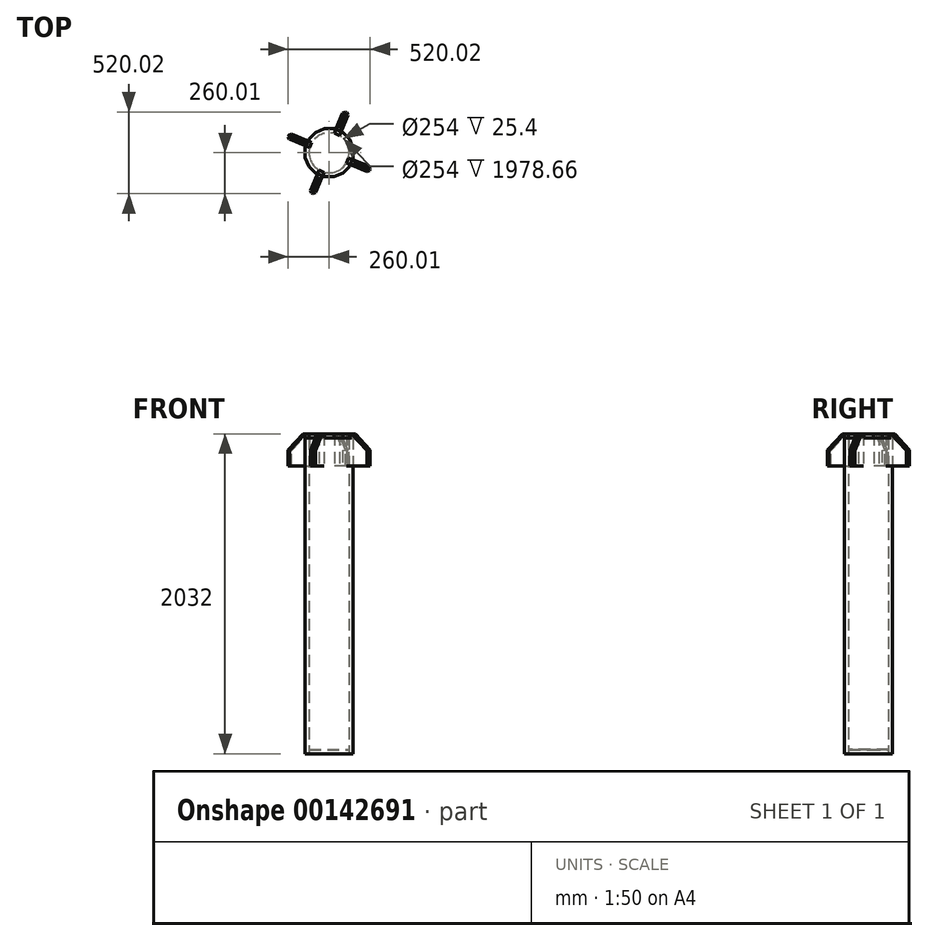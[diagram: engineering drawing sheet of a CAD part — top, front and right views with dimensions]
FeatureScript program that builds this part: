
annotation { "Feature Type Name" : "Feature", "Feature Type Description" : "" }
export const myFeature = defineFeature(function(context is Context, id is Id, definition is map)
    precondition{}
    {
        {
            var Q0;
            Q0=qCreatedBy(makeId("Top.planeOp"),FACE);
            var sketch = newSketch(context, id + "F0", { "sketchPlane" : qUnion([Q0])});
            skCircle(sketch, "E0", {"center": v(0, 0) * mm, "radius": 152.4 * mm});
            skCircle(sketch, "E1", {"center": v(0, 0) * mm, "radius": 151.13 * mm});
            skSolve(sketch);
        }
        {
            var Q0;
            Q0 = qSketchRegion(id + "F0", true);
            var Q1;
            Q1=makeQuery(id+"F0.imprint","IMPRINT",FACE,{"disambiguationData":[TD([[makeQuery(id+"F0.imprint","IMPRINT",EDGE,{"derivedFrom":sQuery(id+"F0.wireOp",EDGE,"E1")}),1.0]])]});
            extrude(context, id + "F1", {"entities" : qUnion([Q0, Q1]), "depth" : 2032 * mm});
        }
        {
            var Q0;
            Q0=makeQuery(id+"F1.opExtrude","CAP_FACE",FACE,{"disambiguationData":[OSD([sQuery(id+"F0.wireOp",EDGE,"E0")])],"isStart":true});
            shell(context, id + "F2", {"entities" : qUnion([Q0]), "thickness" : 25.4 * mm});
        }
        {
            var Q0;
            Q0=makeQuery(id+"F1.opExtrude","CAP_FACE",FACE,{"disambiguationData":[OSD([sQuery(id+"F0.wireOp",EDGE,"E0")])],"isStart":true});
            cPlane(context, id + "F3", {"entities" : qUnion([Q0]), "cplaneType" : CPlaneType.OFFSET, "offset" : 25.4 * mm, "oppositeDirection" : true, "width" : 152.4 * mm, "height" : 152.4 * mm});
        }
        {
            var Q0;
            Q0=qCreatedBy(id+"F3.planeOp",FACE);
            var sketch = newSketch(context, id + "F4", { "sketchPlane" : qUnion([Q0])});
            skCircle(sketch, "E2", {"center": v(0, 0) * mm, "radius": 152.4 * mm});
            skSolve(sketch);
        }
        {
            var Q0;
            Q0 = qSketchRegion(id + "F4", true);
            extrude(context, id + "F5", {"entities" : qUnion([Q0]), "operationType" : NewBodyOperationType.ADD, "oppositeDirection" : true, "depth" : 2.54 * mm});
        }
        {
            var Q0;
            Q0=makeQuery(id+"F1.opExtrude","CAP_FACE",FACE,{"disambiguationData":[OSD([sQuery(id+"F0.wireOp",EDGE,"E0")])],"isStart":false});
            var sketch = newSketch(context, id + "F6", { "sketchPlane" : qUnion([Q0])});
            skCircle(sketch, "E3.cCircle", {"center": v(0, 0) * mm, "radius": 152.4 * mm, "construction": true});
            skLineSegment(sketch, "E3.0", {"start": v(-152.4, -30.31) * mm, "end": v(-152.4, 30.31) * mm});
            skLineSegment(sketch, "E3.1", {"start": v(-152.4, 30.31) * mm, "end": v(-129.2, 86.33) * mm});
            skLineSegment(sketch, "E3.2", {"start": v(-129.2, 86.33) * mm, "end": v(-86.33, 129.2) * mm});
            skLineSegment(sketch, "E3.3", {"start": v(-86.33, 129.2) * mm, "end": v(-30.31, 152.4) * mm});
            skLineSegment(sketch, "E3.4", {"start": v(-30.31, 152.4) * mm, "end": v(30.31, 152.4) * mm});
            skLineSegment(sketch, "E3.5", {"start": v(30.31, 152.4) * mm, "end": v(86.33, 129.2) * mm});
            skLineSegment(sketch, "E3.6", {"start": v(86.33, 129.2) * mm, "end": v(129.2, 86.33) * mm});
            skLineSegment(sketch, "E3.7", {"start": v(129.2, 86.33) * mm, "end": v(152.4, 30.31) * mm});
            skLineSegment(sketch, "E3.8", {"start": v(152.4, 30.31) * mm, "end": v(152.4, -30.31) * mm});
            skLineSegment(sketch, "E3.9", {"start": v(152.4, -30.31) * mm, "end": v(129.2, -86.33) * mm});
            skLineSegment(sketch, "E3.10", {"start": v(129.2, -86.33) * mm, "end": v(86.33, -129.2) * mm});
            skLineSegment(sketch, "E3.11", {"start": v(86.33, -129.2) * mm, "end": v(30.31, -152.4) * mm});
            skLineSegment(sketch, "E3.12", {"start": v(30.31, -152.4) * mm, "end": v(-30.31, -152.4) * mm});
            skLineSegment(sketch, "E3.13", {"start": v(-30.31, -152.4) * mm, "end": v(-86.33, -129.2) * mm});
            skLineSegment(sketch, "E3.14", {"start": v(-86.33, -129.2) * mm, "end": v(-129.2, -86.33) * mm});
            skLineSegment(sketch, "E3.15", {"start": v(-129.2, -86.33) * mm, "end": v(-152.4, -30.31) * mm});
            skPoint(sketch, "E3.0.midPoint", {"position": v(-152.4, 0) * mm});
            skSolve(sketch);
        }
        {
            var Q0;
            Q0 = qSketchRegion(id + "F6", true);
            extrude(context, id + "F7", {"entities" : qUnion([Q0]), "operationType" : NewBodyOperationType.ADD, "oppositeDirection" : true, "depth" : 25.4 * mm});
        }
        {
            var Q0;
            Q0=makeQuery(id+"F7.opExtrude","SWEPT_FACE",FACE,{"disambiguationData":[OSD([sQuery(id+"F6.wireOp",EDGE,"E3.13")])]});
            var sketch = newSketch(context, id + "F8", { "sketchPlane" : qUnion([Q0])});
            skLineSegment(sketch, "E4.bottom", {"start": v(-17.61, 2032) * mm, "end": v(17.61, 2032) * mm});
            skLineSegment(sketch, "E4.top", {"start": v(-17.61, 1828.8) * mm, "end": v(17.61, 1828.8) * mm});
            skLineSegment(sketch, "E4.left", {"start": v(-17.61, 2032) * mm, "end": v(-17.61, 1828.8) * mm});
            skLineSegment(sketch, "E4.right", {"start": v(17.61, 2032) * mm, "end": v(17.61, 1828.8) * mm});
            skSolve(sketch);
        }
        {
            var Q0;
            Q0=makeQuery(id+"F8.imprint","IMPRINT",FACE,{"disambiguationData":[TD([[makeQuery(id+"F8.imprint","IMPRINT",EDGE,{"derivedFrom":sQuery(id+"F8.wireOp",EDGE,"E4.bottom")}),-1.0]])]});
            var Q1;
            {var subQ12=sQuery(id+"F8.wireOp",EDGE,"E4.top");Q1=makeQuery(id+"F8.imprint","IMPRINT",FACE,{"disambiguationData":[TD([[makeQuery(id+"F8.imprint","IMPRINT",EDGE,{"derivedFrom":subQ12}),1.0]])]});}
            var Q2;
            {var subQ12=sQuery(id+"F8.wireOp",EDGE,"E4.bottom");Q2=makeQuery(id+"F8.imprint","IMPRINT",FACE,{"disambiguationData":[TD([[makeQuery(id+"F8.imprint","IMPRINT",EDGE,{"derivedFrom":subQ12}),1.0]])]});}
            extrude(context, id + "F9", {"entities" : qUnion([Q0, Q1, Q2]), "depth" : 127 * mm, "hasSecondDirection" : true, "secondDirectionOppositeDirection" : true, "secondDirectionDepth" : 25.4 * mm});
        }
        {
            var Q0;
            Q0=makeQuery(id+"F9.opExtrude","CAP_EDGE",EDGE,{"disambiguationData":[OSD([sQuery(id+"F8.wireOp",EDGE,"E4.bottom")])],"isStart":false});
            chamfer(context, id + "F10", {"entities" : qUnion([Q0]), "width" : 101.6 * mm, "tangentPropagation" : true});
        }
        {
            var Q0;
            Q0=makeQuery(id+"F10.opChamfer","BLEND_EDGE",EDGE,{"blendedFrom":[makeQuery(id+"F9.opExtrude","CAP_EDGE",EDGE,{"disambiguationData":[OSD([sQuery(id+"F8.wireOp",EDGE,"E4.bottom")])],"isStart":false}),makeQuery(id+"F9.opExtrude","SWEPT_FACE",FACE,{"disambiguationData":[OSD([sQuery(id+"F8.wireOp",EDGE,"E4.right")])]})],"blendedInto":[makeQuery(id+"F9.opExtrude","SWEPT_FACE",FACE,{"disambiguationData":[OSD([sQuery(id+"F8.wireOp",EDGE,"E4.right")])]})]});
            var Q1;
            Q1=makeQuery(id+"F10.opChamfer","BLEND_EDGE",EDGE,{"blendedFrom":[makeQuery(id+"F9.opExtrude","CAP_EDGE",EDGE,{"disambiguationData":[OSD([sQuery(id+"F8.wireOp",EDGE,"E4.bottom")])],"isStart":false}),makeQuery(id+"F9.opExtrude","SWEPT_FACE",FACE,{"disambiguationData":[OSD([sQuery(id+"F8.wireOp",EDGE,"E4.left")])]})],"blendedInto":[makeQuery(id+"F9.opExtrude","SWEPT_FACE",FACE,{"disambiguationData":[OSD([sQuery(id+"F8.wireOp",EDGE,"E4.left")])]})]});
            var Q2;
            Q2=makeQuery(id+"F9.opExtrude","CAP_EDGE",EDGE,{"disambiguationData":[OSD([sQuery(id+"F8.wireOp",EDGE,"E4.right")])],"isStart":false});
            var Q3;
            Q3=makeQuery(id+"F9.opExtrude","CAP_EDGE",EDGE,{"disambiguationData":[OSD([sQuery(id+"F8.wireOp",EDGE,"E4.left")])],"isStart":false});
            chamfer(context, id + "F11", {"entities" : qUnion([Q0, Q1, Q2, Q3]), "width" : 12.7 * mm, "tangentPropagation" : true});
        }
        {
            var Q0;
            Q0=makeQuery(id+"F9.opExtrude","SWEPT_BODY",BODY,{"disambiguationData":[OSD([sQuery(id+"F8.wireOp",EDGE,"E4.bottom"),sQuery(id+"F8.wireOp",EDGE,"E4.top"),sQuery(id+"F8.wireOp",EDGE,"E4.left"),sQuery(id+"F8.wireOp",EDGE,"E4.right")])]});
            var Q1;
            {var subQ0=sQuery(id+"F0.wireOp",EDGE,"E0");Q1=makeQuery(id+"F2.opShell","OFFSET_EDGE",EDGE,{"disambiguationData":[OSD([subQ0]),TDD([makeQuery(id+"F1.opExtrude","CAP_EDGE",EDGE,{"disambiguationData":[OSD([subQ0])],"isStart":true})])]});}
            circularPattern(context, id + "F12", {"entities" : qUnion([Q0]), "axis" : qUnion([Q1]), "angle" : 360 * degree, "instanceCount" : 4, "equalSpace" : true});
        }
    });
